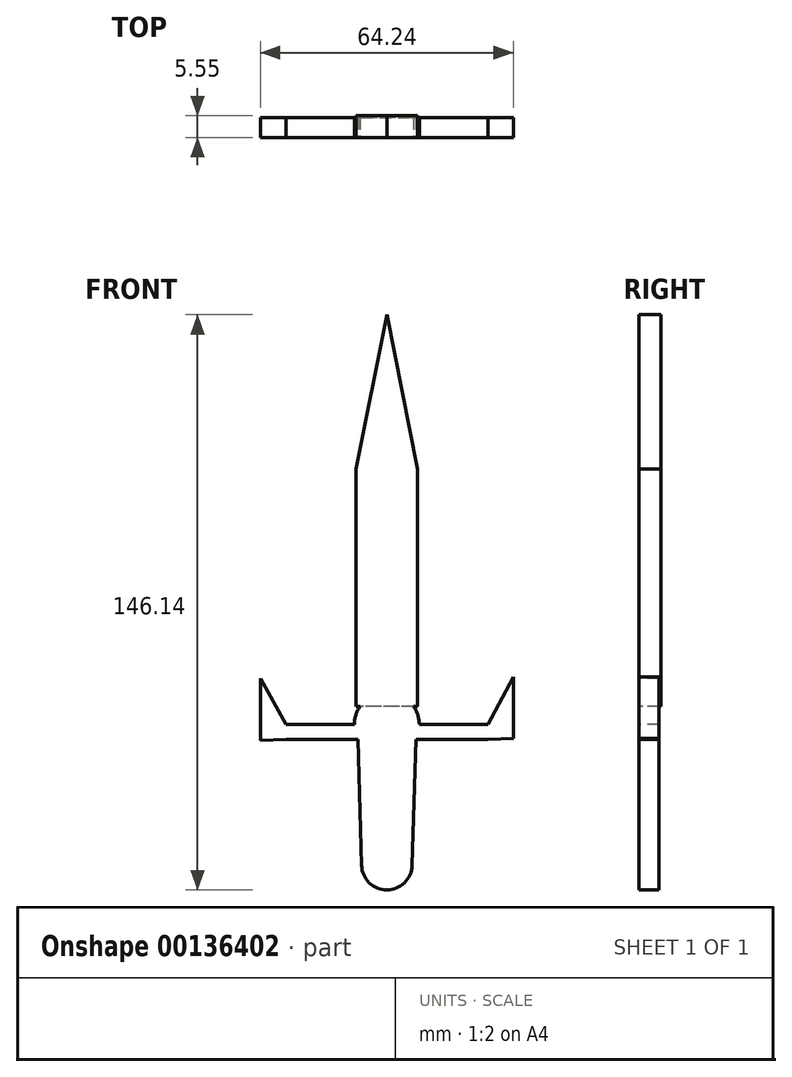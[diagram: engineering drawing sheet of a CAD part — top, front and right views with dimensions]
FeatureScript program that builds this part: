
annotation { "Feature Type Name" : "Feature", "Feature Type Description" : "" }
export const myFeature = defineFeature(function(context is Context, id is Id, definition is map)
    precondition{}
    {
        {
            var Q0;
            Q0=qCreatedBy(makeId("Front.planeOp"),FACE);
            var sketch = newSketch(context, id + "F0", { "sketchPlane" : qUnion([Q0])});
            skCircle(sketch, "E0", {"center": v(0, 0) * mm, "radius": 8.24 * mm});
            skLineSegment(sketch, "E1", {"start": v(0, 0) * mm, "end": v(-25.66, 0) * mm});
            skLineSegment(sketch, "E2", {"start": v(0, -35.55) * mm, "end": v(-2.55, -35.55) * mm});
            skLineSegment(sketch, "E3", {"start": v(-2.55, -35.55) * mm, "end": v(2.74, -35.55) * mm});
            skLineSegment(sketch, "E4", {"start": v(-25.66, 0) * mm, "end": v(-25.66, -3.7) * mm});
            skLineSegment(sketch, "E5", {"start": v(-25.66, -3.7) * mm, "end": v(-7.37, -3.7) * mm});
            skLineSegment(sketch, "E6", {"start": v(7.37, -3.7) * mm, "end": v(25.67, -3.7) * mm});
            skLineSegment(sketch, "E7", {"start": v(25.67, -3.7) * mm, "end": v(25.67, 0) * mm});
            skLineSegment(sketch, "E8", {"start": v(0, 0) * mm, "end": v(25.67, 0) * mm});
            skCircle(sketch, "E9", {"center": v(0, -35.55) * mm, "radius": 6.42 * mm});
            skLineSegment(sketch, "E10", {"start": v(-7.37, -3.7) * mm, "end": v(-6.42, -35.74) * mm});
            skLineSegment(sketch, "E11", {"start": v(6.42, -35.74) * mm, "end": v(7.37, -3.7) * mm});
            skLineSegment(sketch, "E12", {"start": v(-25.66, 0) * mm, "end": v(-32.12, 11.72) * mm});
            skLineSegment(sketch, "E13", {"start": v(-32.12, 11.72) * mm, "end": v(-32.12, -3.95) * mm});
            skLineSegment(sketch, "E14", {"start": v(-32.12, -3.95) * mm, "end": v(-25.66, -3.7) * mm});
            skLineSegment(sketch, "E15", {"start": v(25.67, 0) * mm, "end": v(32.12, 12.12) * mm});
            skLineSegment(sketch, "E16", {"start": v(32.12, 12.12) * mm, "end": v(32.12, -3.55) * mm});
            skLineSegment(sketch, "E17", {"start": v(32.12, -3.55) * mm, "end": v(25.67, -3.7) * mm});
            skSolve(sketch);
        }
        {
            var Q0;
            Q0 = qSketchRegion(id + "F0", true);
            extrude(context, id + "F1", {"entities" : qUnion([Q0]), "oppositeDirection" : true, "depth" : 5.05 * mm});
        }
        {
            var Q0;
            Q0=qCreatedBy(makeId("Front.planeOp"),FACE);
            var sketch = newSketch(context, id + "F2", { "sketchPlane" : qUnion([Q0])});
            skLineSegment(sketch, "E18", {"start": v(7.83, 65) * mm, "end": v(-7.83, 65) * mm});
            skLineSegment(sketch, "E19", {"start": v(7.83, 65) * mm, "end": v(0, 104.17) * mm});
            skPoint(sketch, "E19.endSnap0", {"position": v(0, 65) * mm});
            skLineSegment(sketch, "E20", {"start": v(0, 104.17) * mm, "end": v(-7.83, 65) * mm});
            skLineSegment(sketch, "E21", {"start": v(7.83, 4.67) * mm, "end": v(-7.83, 4.67) * mm});
            skLineSegment(sketch, "E22", {"start": v(-7.83, 4.67) * mm, "end": v(-7.83, 27) * mm});
            skLineSegment(sketch, "E23", {"start": v(-7.83, 27) * mm, "end": v(0, 27) * mm});
            skLineSegment(sketch, "E24", {"start": v(7.83, 4.67) * mm, "end": v(7.83, 27) * mm});
            skLineSegment(sketch, "E25", {"start": v(7.83, 27) * mm, "end": v(0, 27) * mm});
            skLineSegment(sketch, "E26", {"start": v(-7.83, 65) * mm, "end": v(-7.83, 43.94) * mm});
            skLineSegment(sketch, "E27", {"start": v(-7.83, 43.94) * mm, "end": v(7.83, 43.94) * mm});
            skLineSegment(sketch, "E28", {"start": v(7.83, 43.94) * mm, "end": v(7.83, 65) * mm});
            skLineSegment(sketch, "E29", {"start": v(-7.83, 43.94) * mm, "end": v(-7.83, 27) * mm});
            skLineSegment(sketch, "E30", {"start": v(7.83, 43.94) * mm, "end": v(7.83, 27) * mm});
            skSolve(sketch);
        }
        {
            var Q0;
            Q0=makeQuery(id+"F2.imprint","IMPRINT",FACE,{"disambiguationData":[TD([[makeQuery(id+"F2.imprint","IMPRINT",EDGE,{"derivedFrom":sQuery(id+"F2.wireOp",EDGE,"E18")}),-1.0]])]});
            var Q1;
            Q1=makeQuery(id+"F2.imprint","IMPRINT",FACE,{"disambiguationData":[TD([[makeQuery(id+"F2.imprint","IMPRINT",EDGE,{"derivedFrom":sQuery(id+"F2.wireOp",EDGE,"VKojrlel-Oh3j-utAw-bhfY-GcajCSgJtgfT")}),1.0]])]});
            var Q2;
            Q2=makeQuery(id+"F2.imprint","IMPRINT",FACE,{"disambiguationData":[TD([[makeQuery(id+"F2.imprint","IMPRINT",EDGE,{"derivedFrom":sQuery(id+"F2.wireOp",EDGE,"E18")}),1.0]])]});
            var Q3;
            Q3=makeQuery(id+"F2.imprint","IMPRINT",FACE,{"disambiguationData":[TD([[makeQuery(id+"F2.imprint","IMPRINT",EDGE,{"derivedFrom":sQuery(id+"F2.wireOp",EDGE,"E21")}),-1.0]])]});
            var Q4;
            {var subQ0=sQuery(id+"F2.wireOp",EDGE,"E27");Q4=makeQuery(id+"F2.imprint","IMPRINT",FACE,{"disambiguationData":[TD([[makeQuery(id+"F2.imprint","IMPRINT",EDGE,{"derivedFrom":subQ0}),1.0]])]});}
            var Q5;
            {var subQ0=sQuery(id+"F2.wireOp",EDGE,"E30");var subQ1=sQuery(id+"F2.wireOp",EDGE,"cTvzdMO7-sSfm-VeVS-Cqcs-JjhteEmcdoQZ");var subQ3=makeQuery(id+"F2.imprint","INTERSECT",VERTEX,{"derivedFrom":[subQ1,subQ0]});Q5=makeQuery(id+"F2.imprint","IMPRINT",FACE,{"disambiguationData":[TD([[makeQuery(id+"F2.imprint","IMPRINT",EDGE,{"disambiguationData":[TD([[subQ3,-1.0]])],"derivedFrom":subQ1}),1.0]])]});}
            var Q6;
            {var subQ10=sQuery(id+"F2.wireOp",EDGE,"E27");Q6=makeQuery(id+"F2.imprint","IMPRINT",FACE,{"disambiguationData":[TD([[makeQuery(id+"F2.imprint","IMPRINT",EDGE,{"derivedFrom":subQ10}),-1.0]])]});}
            var Q7;
            {var subQ0=sQuery(id+"F2.wireOp",EDGE,"E29");var subQ1=sQuery(id+"F2.wireOp",EDGE,"cTvzdMO7-sSfm-VeVS-Cqcs-JjhteEmcdoQZ");var subQ3=makeQuery(id+"F2.imprint","INTERSECT",VERTEX,{"derivedFrom":[subQ1,subQ0]});Q7=makeQuery(id+"F2.imprint","IMPRINT",FACE,{"disambiguationData":[TD([[makeQuery(id+"F2.imprint","IMPRINT",EDGE,{"disambiguationData":[TD([[subQ3,1.0]])],"derivedFrom":subQ1}),1.0]])]});}
            extrude(context, id + "F3", {"entities" : qUnion([Q0, Q1, Q2, Q3, Q4, Q5, Q6, Q7]), "operationType" : NewBodyOperationType.ADD, "oppositeDirection" : true, "depth" : 5.55 * mm});
        }
    });
